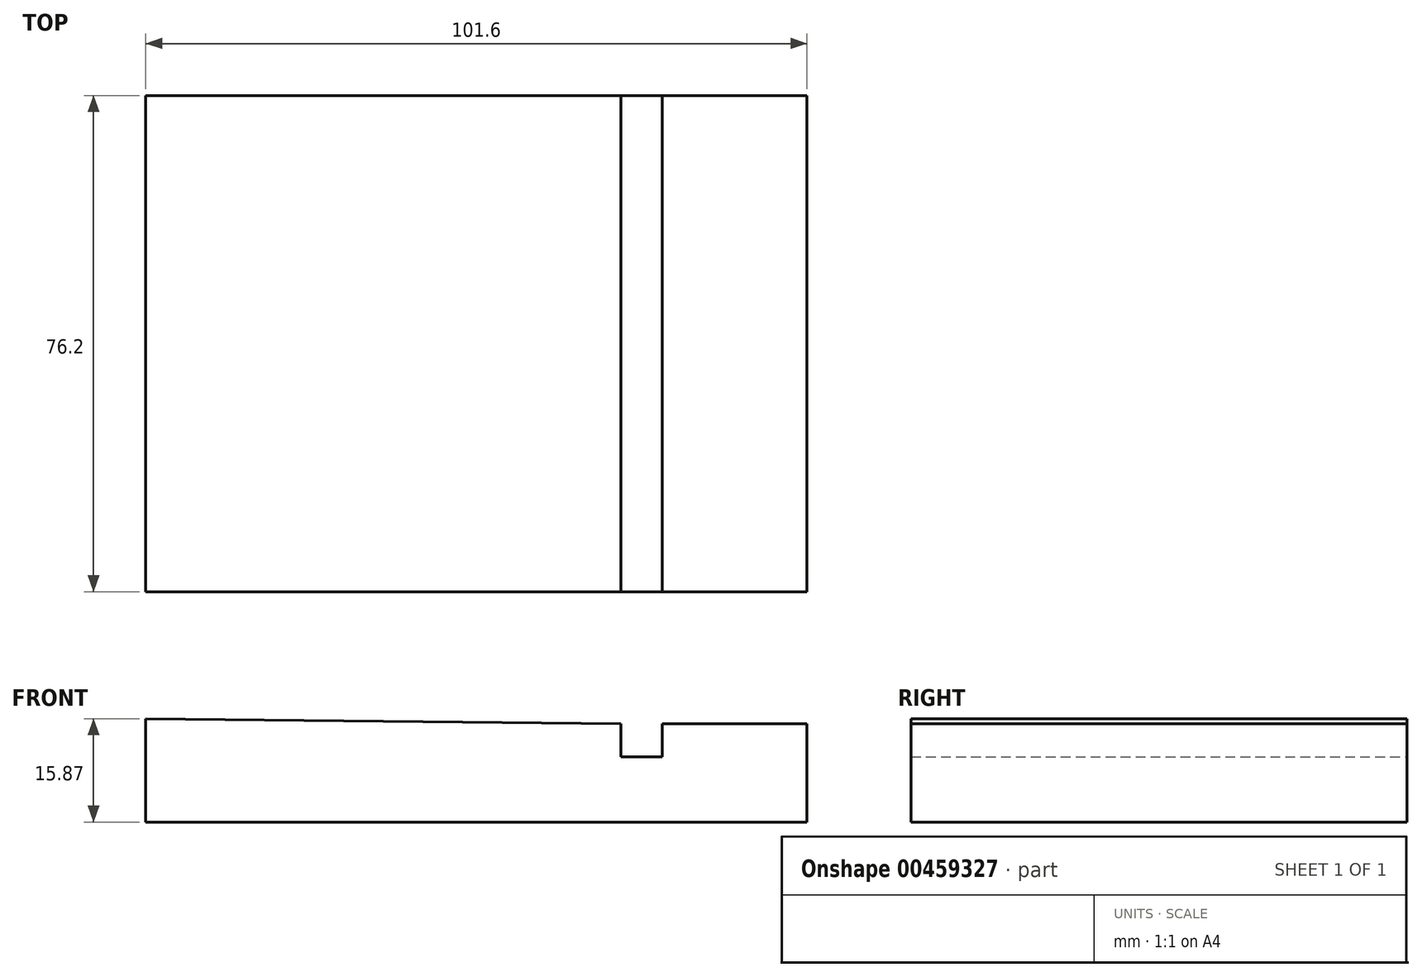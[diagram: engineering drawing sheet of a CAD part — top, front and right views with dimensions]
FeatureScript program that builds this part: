
annotation { "Feature Type Name" : "Feature", "Feature Type Description" : "" }
export const myFeature = defineFeature(function(context is Context, id is Id, definition is map)
    precondition{}
    {
        {
            var Q0;
            Q0=qCreatedBy(makeId("Front.planeOp"),FACE);
            var sketch = newSketch(context, id + "F0", { "sketchPlane" : qUnion([Q0])});
            skLineSegment(sketch, "E0", {"start": v(-67.48, 7.85) * mm, "end": v(-67.48, -8.02) * mm});
            skLineSegment(sketch, "E1", {"start": v(-67.48, -8.02) * mm, "end": v(34.12, -8.02) * mm});
            skLineSegment(sketch, "E2", {"start": v(34.12, -8.02) * mm, "end": v(34.12, 7.06) * mm});
            skLineSegment(sketch, "E3", {"start": v(34.12, 7.06) * mm, "end": v(11.9, 7.06) * mm});
            skLineSegment(sketch, "E4", {"start": v(11.9, 7.06) * mm, "end": v(11.9, 1.98) * mm});
            skLineSegment(sketch, "E5", {"start": v(11.9, 1.98) * mm, "end": v(5.55, 1.98) * mm});
            skLineSegment(sketch, "E6", {"start": v(5.55, 1.98) * mm, "end": v(5.55, 7.06) * mm});
            skLineSegment(sketch, "E7", {"start": v(5.55, 7.06) * mm, "end": v(-67.48, 7.85) * mm});
            skSolve(sketch);
        }
        {
            var Q0;
            Q0=makeQuery(id+"F0.imprint","IMPRINT",FACE,{"disambiguationData":[TD([[makeQuery(id+"F0.imprint","IMPRINT",EDGE,{"derivedFrom":sQuery(id+"F0.wireOp",EDGE,"E0")}),1.0]])]});
            extrude(context, id + "F1", {"entities" : qUnion([Q0]), "depth" : 76.2 * mm});
        }
    });
